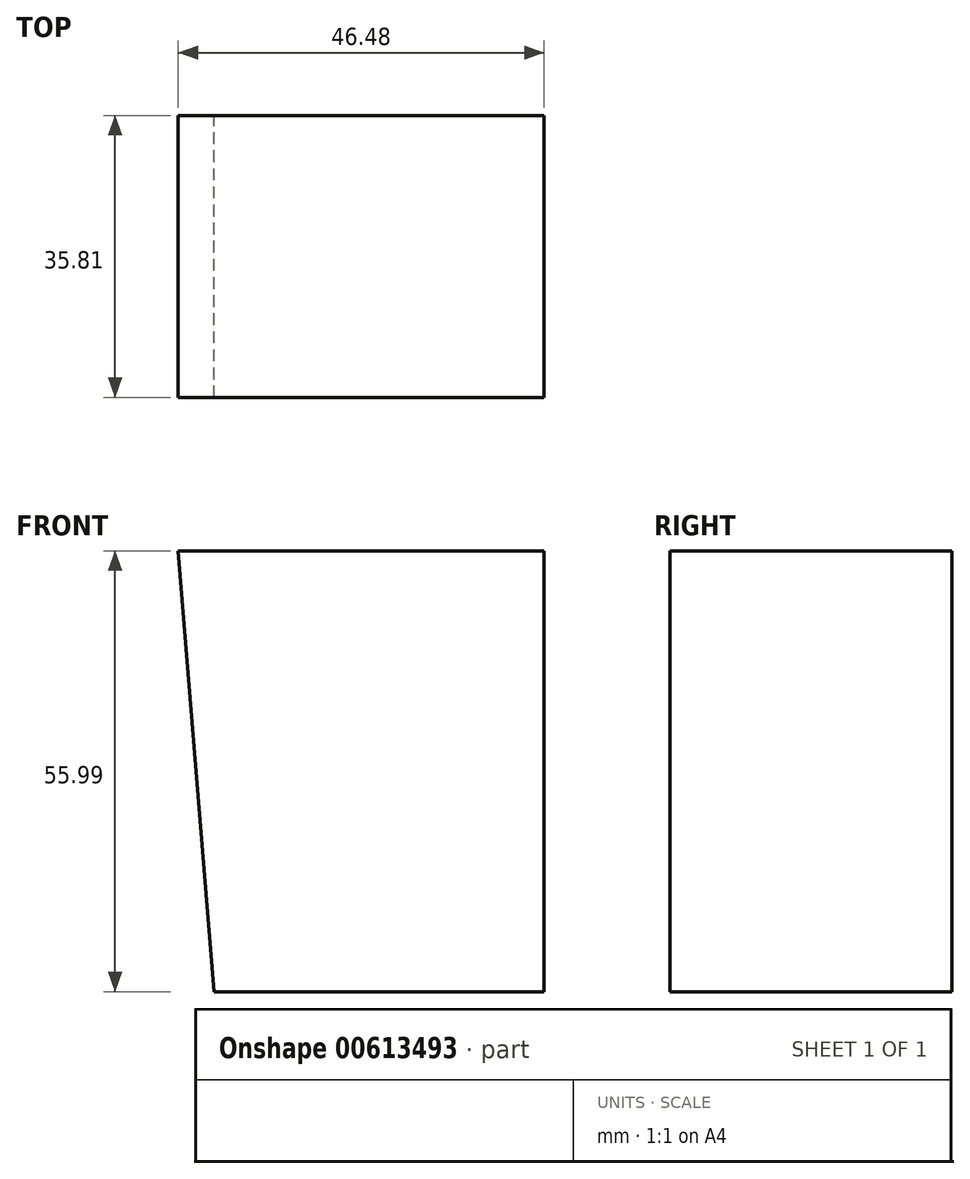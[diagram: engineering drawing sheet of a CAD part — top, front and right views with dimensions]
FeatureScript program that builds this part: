
annotation { "Feature Type Name" : "Feature", "Feature Type Description" : "" }
export const myFeature = defineFeature(function(context is Context, id is Id, definition is map)
    precondition{}
    {
        {
            var Q0;
            Q0=qCreatedBy(makeId("Front.planeOp"),FACE);
            var sketch = newSketch(context, id + "F0", { "sketchPlane" : qUnion([Q0])});
            skLineSegment(sketch, "E0", {"start": v(0, 0) * mm, "end": v(-41.92, 0) * mm});
            skLineSegment(sketch, "E1", {"start": v(-41.92, 0) * mm, "end": v(-46.48, 56) * mm});
            skLineSegment(sketch, "E2", {"start": v(-46.48, 56) * mm, "end": v(0, 56) * mm});
            skLineSegment(sketch, "E3", {"start": v(0, 56) * mm, "end": v(0, 0) * mm});
            skLineSegment(sketch, "E4", {"start": v(-41.92, 0) * mm, "end": v(-54.97, 0) * mm});
            skSolve(sketch);
        }
        {
            var Q0;
            Q0 = qSketchRegion(id + "F0", true);
            var Q1;
            Q1=makeQuery(id+"F0.imprint","IMPRINT",FACE,{"disambiguationData":[TD([[makeQuery(id+"F0.imprint","IMPRINT",EDGE,{"derivedFrom":sQuery(id+"F0.wireOp",EDGE,"E0")}),-1.0]])]});
            extrude(context, id + "F1", {"entities" : qUnion([Q0, Q1]), "depth" : 35.81 * mm, "offsetDistance" : 25.4 * mm});
        }
    });
